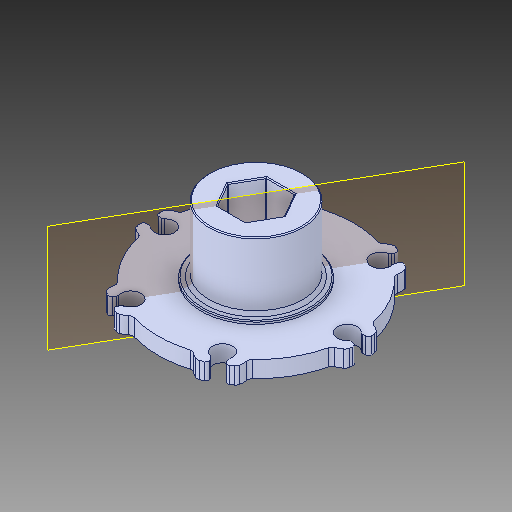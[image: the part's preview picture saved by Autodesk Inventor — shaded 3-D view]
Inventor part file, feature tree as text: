
AUTODESK INVENTOR PART (.ipt)
format: ipt  version: 2018 (Build 220112000, 112)  size: 351,744 bytes
history: native  units: in
note: dims shown in document units (in); Inventor stores cm internally (conversion verified against a paired STEP export)
features: plane x1, fillet x1
ambient origin geometry x8: Origin, YZ Plane, XZ Plane, XY Plane, X Axis, Y Axis, Z Axis, Center Point
bodies: Solid1 (feature_tree)
feature tree (2):
  plane  "Work Plane1"
  fillet  "Fillet7"  [1 undecoded]
note: 1 required parameter value undecoded (feature->parameter linkage not recoverable at this tier; creation-order binding heuristic only, values carry confidence <= 0.55)
